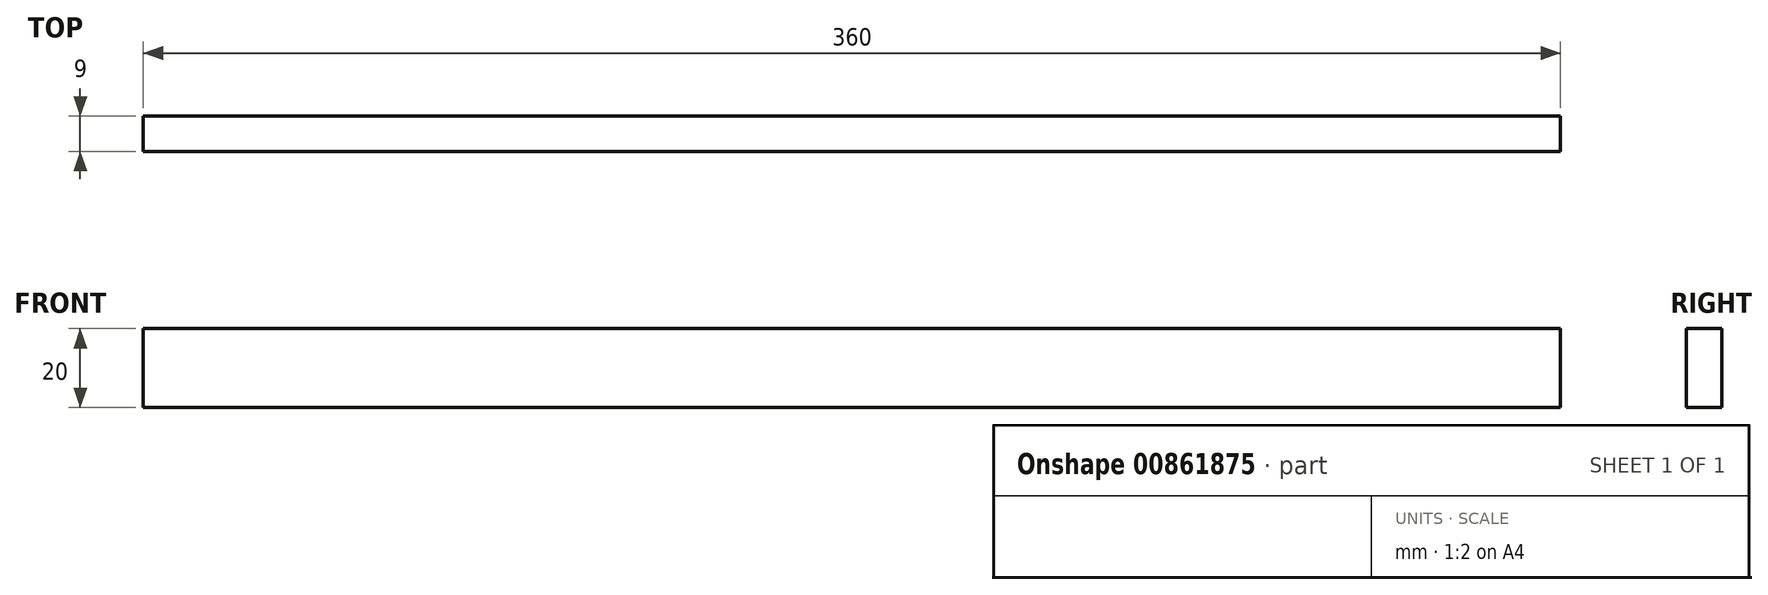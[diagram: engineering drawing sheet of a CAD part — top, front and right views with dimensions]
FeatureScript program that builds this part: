
annotation { "Feature Type Name" : "Feature", "Feature Type Description" : "" }
export const myFeature = defineFeature(function(context is Context, id is Id, definition is map)
    precondition{}
    {
        {
            var Q0;
            Q0=qCreatedBy(makeId("Front.planeOp"),FACE);
            var sketch = newSketch(context, id + "F0", { "sketchPlane" : qUnion([Q0])});
            skLineSegment(sketch, "E0.bottom", {"start": v(-179.4, 10.91) * mm, "end": v(180.6, 10.91) * mm});
            skLineSegment(sketch, "E0.top", {"start": v(-179.4, -9.09) * mm, "end": v(180.6, -9.09) * mm});
            skLineSegment(sketch, "E0.left", {"start": v(-179.4, 10.91) * mm, "end": v(-179.4, -9.09) * mm});
            skLineSegment(sketch, "E0.right", {"start": v(180.6, 10.91) * mm, "end": v(180.6, -9.09) * mm});
            skSolve(sketch);
        }
        {
            var Q0;
            Q0 = qSketchRegion(id + "F0", true);
            extrude(context, id + "F1", {"entities" : qUnion([Q0]), "depth" : 9 * mm, "offsetDistance" : 25 * mm});
        }
    });
